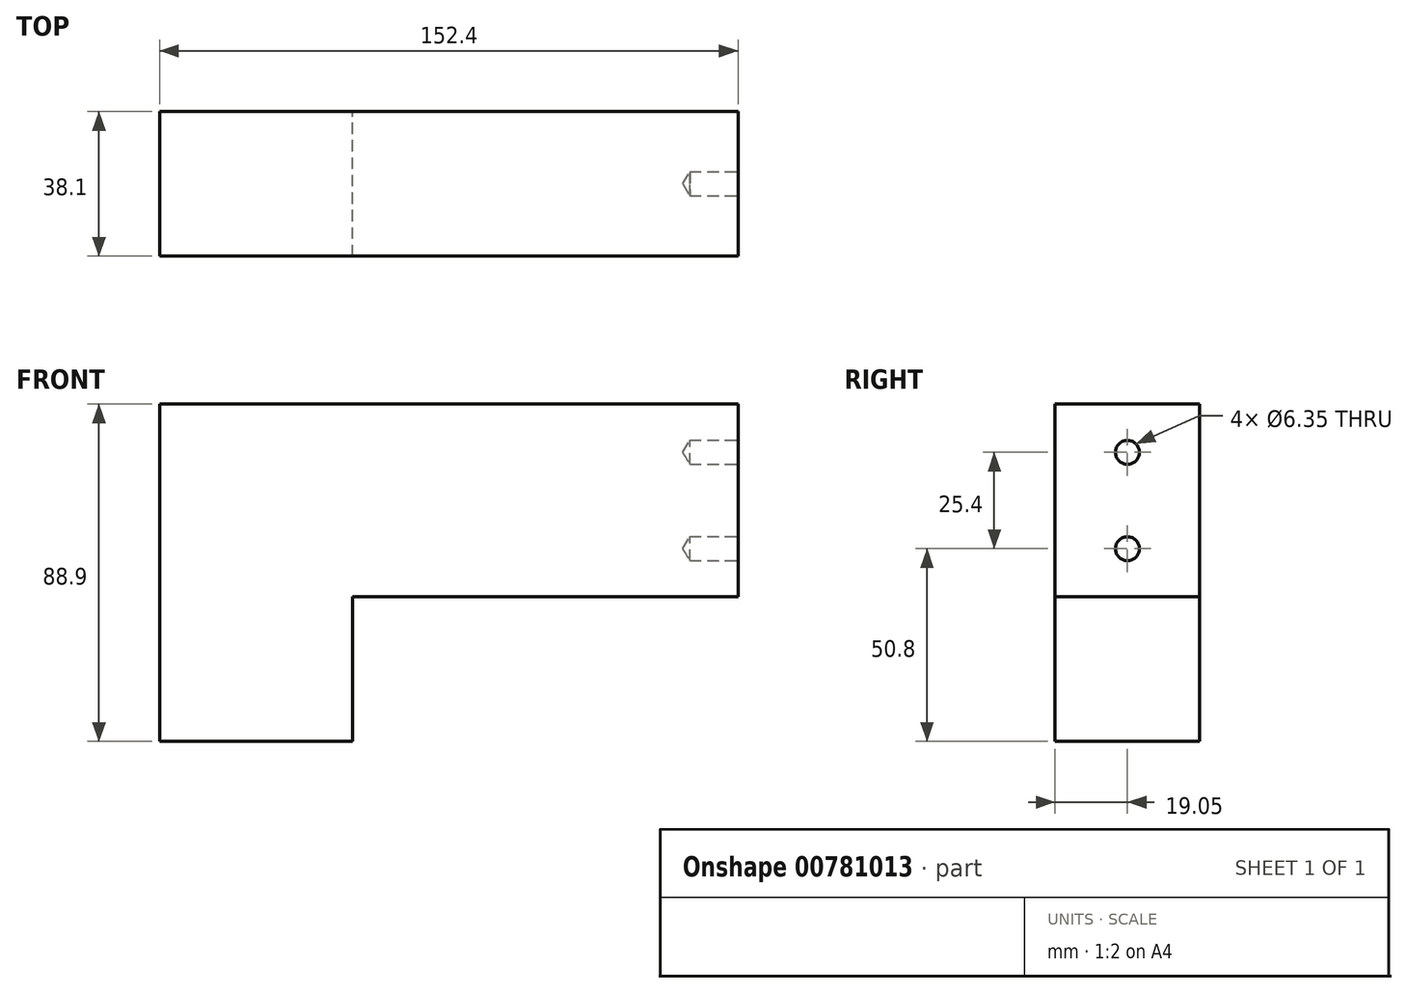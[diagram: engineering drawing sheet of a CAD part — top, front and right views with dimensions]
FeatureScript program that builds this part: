
annotation { "Feature Type Name" : "Feature", "Feature Type Description" : "" }
export const myFeature = defineFeature(function(context is Context, id is Id, definition is map)
    precondition{}
    {
        {
            var Q0;
            Q0=qCreatedBy(makeId("Front.planeOp"),FACE);
            var sketch = newSketch(context, id + "F0", { "sketchPlane" : qUnion([Q0])});
            skLineSegment(sketch, "E0.bottom", {"start": v(0, 0) * mm, "end": v(-152.4, 0) * mm});
            skLineSegment(sketch, "E0.top", {"start": v(-101.6, -88.9) * mm, "end": v(-152.4, -88.9) * mm});
            skLineSegment(sketch, "E0.left", {"start": v(0, 0) * mm, "end": v(0, -50.8) * mm});
            skLineSegment(sketch, "E0.right", {"start": v(-152.4, 0) * mm, "end": v(-152.4, -88.9) * mm});
            skLineSegment(sketch, "E1", {"start": v(-101.6, -88.9) * mm, "end": v(-101.6, -50.8) * mm});
            skLineSegment(sketch, "E2", {"start": v(-101.6, -50.8) * mm, "end": v(0, -50.8) * mm});
            skSolve(sketch);
        }
        {
            var Q0;
            Q0=makeQuery(id+"F0.imprint","IMPRINT",FACE,{"disambiguationData":[TD([[makeQuery(id+"F0.imprint","IMPRINT",EDGE,{"derivedFrom":sQuery(id+"F0.wireOp",EDGE,"E0.bottom")}),1.0]])]});
            extrude(context, id + "F1", {"entities" : qUnion([Q0]), "depth" : 38.1 * mm, "offsetDistance" : 25.4 * mm});
        }
        {
            var Q0;
            Q0=makeQuery(id+"F1.opExtrude","SWEPT_FACE",FACE,{"disambiguationData":[OSD([sQuery(id+"F0.wireOp",EDGE,"E0.left")])]});
            var sketch = newSketch(context, id + "F2", { "sketchPlane" : qUnion([Q0])});
            skLineSegment(sketch, "E3", {"start": v(-19.05, -50.8) * mm, "end": v(-19.05, 0) * mm, "construction": true});
            skPoint(sketch, "E4", {"position": v(-19.05, -38.1) * mm});
            skPoint(sketch, "E5", {"position": v(-19.05, -12.7) * mm});
            skSolve(sketch);
        }
        {
            var Q0;
            Q0=sQuery(id+"F2.wireOp",VERTEX,"E5");
            var Q1;
            Q1=sQuery(id+"F2.wireOp",VERTEX,"E4");
            var Q2;
            Q2=makeQuery(id+"F1.opExtrude","SWEPT_BODY",BODY,{"disambiguationData":[OSD([sQuery(id+"F0.wireOp",EDGE,"E0.bottom"),sQuery(id+"F0.wireOp",EDGE,"E0.top"),sQuery(id+"F0.wireOp",EDGE,"E0.left"),sQuery(id+"F0.wireOp",EDGE,"E0.right"),sQuery(id+"F0.wireOp",EDGE,"E1"),sQuery(id+"F0.wireOp",EDGE,"E2")])]});
            hole(context, id + "F3", {"style" : HoleStyle.SIMPLE, "endStyle" : HoleEndStyle.BLIND, "holeDiameter" : 6.35 * mm, "majorDiameter" : 6.35 * mm, "holeDepth" : 12.7 * mm, "isTappedThrough" : true, "tappedDepth" : 12.7 * mm, "tapClearance" : 3, "locations" : qUnion([Q0, Q1]), "scope" : qUnion([Q2])});
        }
    });
